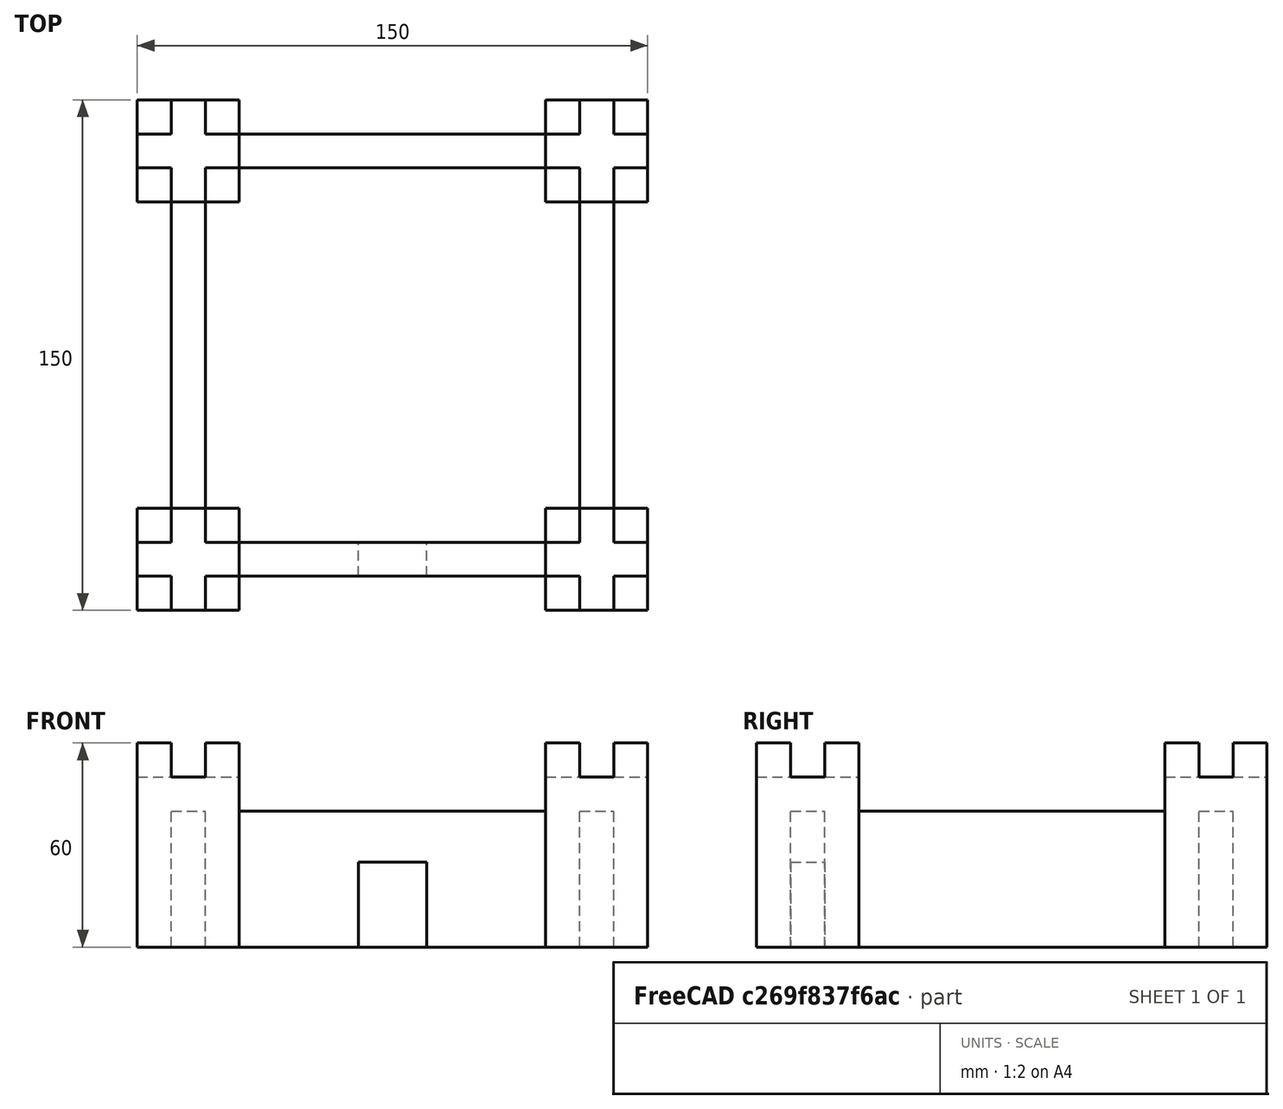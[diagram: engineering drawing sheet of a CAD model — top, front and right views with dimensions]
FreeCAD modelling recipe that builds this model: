
FCSTD DOCUMENT  (FreeCAD 0.16R6707 (Git))
Label: castillo
License: All rights reserved
LicenseURL: http://en.wikipedia.org/wiki/All_rights_reserved
objects: Part::Box×10, Part::Feature×3, Part::MultiFuse×2, Part::Cut×1
note: 16 computed .brp shape members not serialized (recipe doc carries the construction recipe); baked Part::Feature solids carry a one-line shape summary decoded from their .brp

FEATURE [Part::Box] Box  label="Cubo"
  Height = 50
  Length = 30
  Width = 30
FEATURE [Part::Box] Box001  label="Cubo001"
  Height = 10
  Length = 10
  Placement = pos=(0,0,50) rot=(0,0,1;0rad)
  Width = 10
FEATURE [Part::Box] Box002  label="Cubo002"
  Height = 10
  Length = 10
  Placement = pos=(20,0,50) rot=(0,0,1;0rad)
  Width = 10
FEATURE [Part::Box] Box003  label="Cubo003"
  Height = 10
  Length = 10
  Placement = pos=(20,20,50) rot=(0,0,1;0rad)
  Width = 10
FEATURE [Part::Box] Box004  label="Cubo004"
  Height = 10
  Length = 10
  Placement = pos=(0,20,50) rot=(0,0,1;0rad)
  Width = 10
FEATURE [Part::MultiFuse] Fusion  label="Torre"
  Shapes = -> [Box,Box004,Box003,Box002,Box001]
FEATURE [Part::Feature] Fusion001  label="Torre001"
  Placement = pos=(120,0,0) rot=(0,0,1;0rad)
  shape: bbox 30 x 30 x 60 mm, 18 faces (baked)
FEATURE [Part::Feature] Fusion002  label="Torre002"
  Placement = pos=(0,120,0) rot=(0,0,1;0rad)
  shape: bbox 30 x 30 x 60 mm, 18 faces (baked)
FEATURE [Part::Feature] Fusion001001  label="Torre003"
  Placement = pos=(120,120,0) rot=(0,0,1;0rad)
  shape: bbox 30 x 30 x 60 mm, 18 faces (baked)
FEATURE [Part::Box] Box005  label="Cubo005"
  Height = 40
  Length = 90
  Placement = pos=(30,10,0) rot=(0,0,1;0rad)
  Width = 10
FEATURE [Part::Box] Box006  label="Cubo006"
  Height = 40
  Length = 90
  Placement = pos=(30,130,0) rot=(0,0,1;0rad)
  Width = 10
FEATURE [Part::Box] Box007  label="Cubo007"
  Height = 40
  Length = 10
  Placement = pos=(10,30,0) rot=(0,0,1;0rad)
  Width = 90
FEATURE [Part::Box] Box008  label="Cubo008"
  Height = 40
  Length = 10
  Placement = pos=(130,30,0) rot=(0,0,1;0rad)
  Width = 90
FEATURE [Part::Box] Box009  label="Cubo009"
  Height = 25
  Length = 20
  Placement = pos=(65,0,0) rot=(0,0,1;0rad)
  Width = 30
FEATURE [Part::Cut] Cut
  Base = -> Box005
  Tool = -> Box009
FEATURE [Part::MultiFuse] Fusion001002  label="Castillo-final"
  Shapes = -> [Fusion,Fusion001,Fusion002,Fusion001001,Box006,Box007,Box008,Cut]
